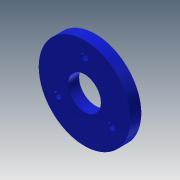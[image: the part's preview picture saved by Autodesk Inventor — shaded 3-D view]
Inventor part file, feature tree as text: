
AUTODESK INVENTOR PART (.ipt)
format: ipt  version: 2013 (Build 170138000, 138)  size: 87,552 bytes
history: native  units: mm
features: extrude x1, sketch x1
ambient origin geometry x8: Origin, YZ Plane, XZ Plane, XY Plane, X Axis, Y Axis, Z Axis, Center Point
bodies: Solid1 (feature_tree)
feature tree (2):
  extrude  "Extrusion1"  [1 undecoded]
  sketch  "Sketch1"  dims[d13=5.0mm d14=0.0mm]
note: 1 required parameter value undecoded (feature->parameter linkage not recoverable at this tier; creation-order binding heuristic only, values carry confidence <= 0.55)
